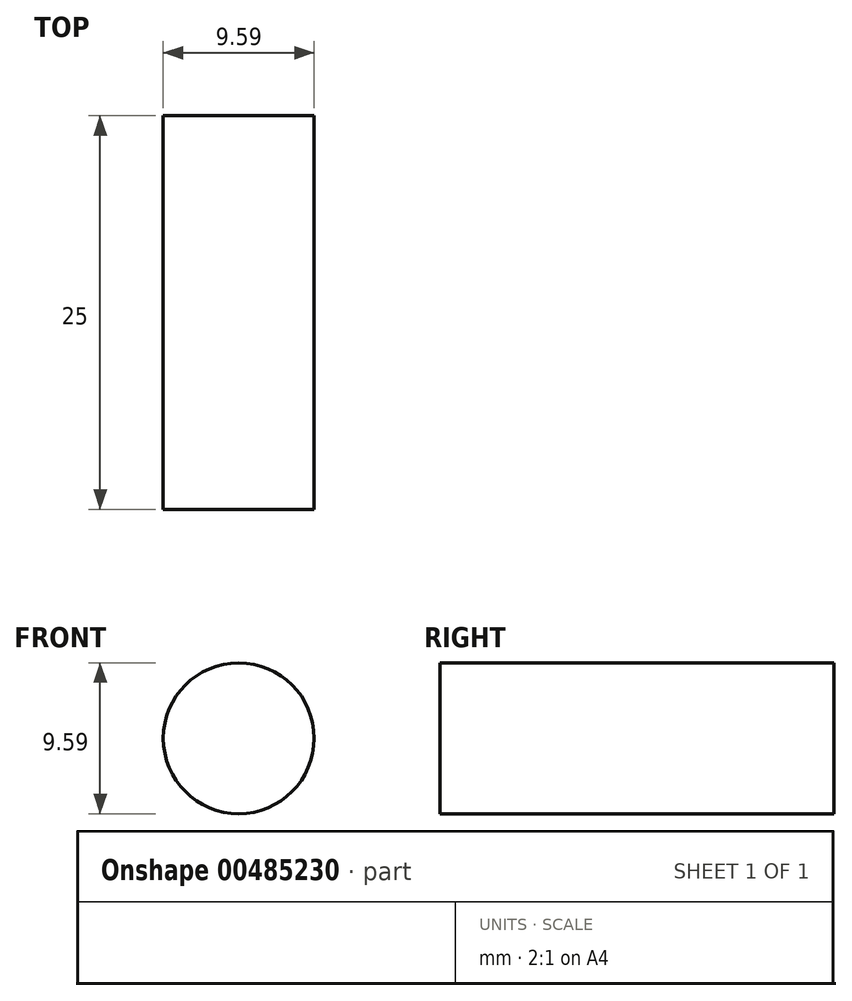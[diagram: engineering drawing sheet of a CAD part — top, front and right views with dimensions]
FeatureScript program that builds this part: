
annotation { "Feature Type Name" : "Feature", "Feature Type Description" : "" }
export const myFeature = defineFeature(function(context is Context, id is Id, definition is map)
    precondition{}
    {
        {
            var Q0;
            Q0=qCreatedBy(makeId("Front.planeOp"),FACE);
            var sketch = newSketch(context, id + "F0", { "sketchPlane" : qUnion([Q0])});
            skCircle(sketch, "E0", {"center": v(-68.03, 47.44) * mm, "radius": 4.8 * mm});
            skSolve(sketch);
        }
        {
            var Q0;
            Q0 = qSketchRegion(id + "F0", true);
            extrude(context, id + "F1", {"entities" : qUnion([Q0]), "depth" : 25 * mm});
        }
    });
